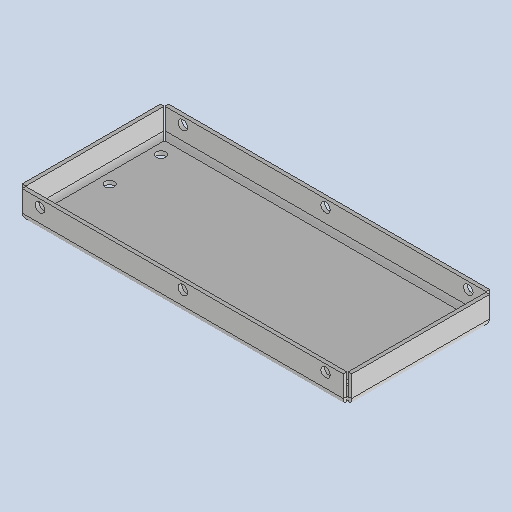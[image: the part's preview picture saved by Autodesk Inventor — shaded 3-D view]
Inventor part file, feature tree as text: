
AUTODESK INVENTOR PART (.ipt)
format: ipt  version: 2025 (Build 290162010, 162A)  size: 286,720 bytes
history: native  units: mm
features: sketch x6, other x5, sheet_metal_op x4, pattern_linear x3, extrude x2, mirror x1, projected_geometry x1
ambient origin geometry x8: Origin, YZ Plane, XZ Plane, XY Plane, X Axis, Y Axis, Z Axis, Center Point
bodies: Solid1 (feature_tree)
feature tree (22):
  sheet_metal_op  "Face1"
  sheet_metal_op  "Flange2"
  extrude  "Extrusion2"  Depth=5.0mm
  pattern_linear  "Rectangular Pattern1"  Count1=20  [1 undecoded]
  extrude  "Extrusion3"  Depth=5.0mm
  pattern_linear  "Rectangular Pattern2"  Count1=4 Spacing1=90.0deg
  pattern_linear  "Rectangular Pattern3"  Count1=2  [1 undecoded]
  mirror  "Mirror1"
  sketch  "Sketch1"  dims[d2=5.0mm d25=450.0mm d26=200.0mm]
  other  "Plate1"
  sketch  "Sketch5"  dims[d27=5.0mm d28=2.5mm]
  other  "Plate3"
  sheet_metal_op  "Bend2"
  sheet_metal_op  "Corner2"
  sketch  "Sketch6"  dims[d29=10.0mm]
  sketch  "Sketch7"  dims[d30=6.0mm d31=40.0mm d32=90.0deg d33=6.0mm d34=20.0mm]
  projected_geometry  "Projected Loop2"
  sketch  "Sketch8"  dims[d35=1.0mm d36=6.0mm]
  sketch  "Sketch9"  dims[d37=30.0mm d38=150.0mm d39=5.0mm d40=0.0mm d41=13.0mm d42=25.0mm d43=0.0mm d44=0.0mm d45=30.0mm d47=195.0mm d48=13.0mm d49=25.0mm d50=0.0mm d51=0.0mm d52=30.0mm d54=70.0mm d55=13.0mm d56=25.0mm d57=5.0mm d58=0.0mm d59=30.0mm d61=70.0mm]
  other  "Cut1"
  other  "Cut2"
  other  "Definition1"
note: 2 required parameter values undecoded (feature->parameter linkage not recoverable at this tier; creation-order binding heuristic only, values carry confidence <= 0.55)
